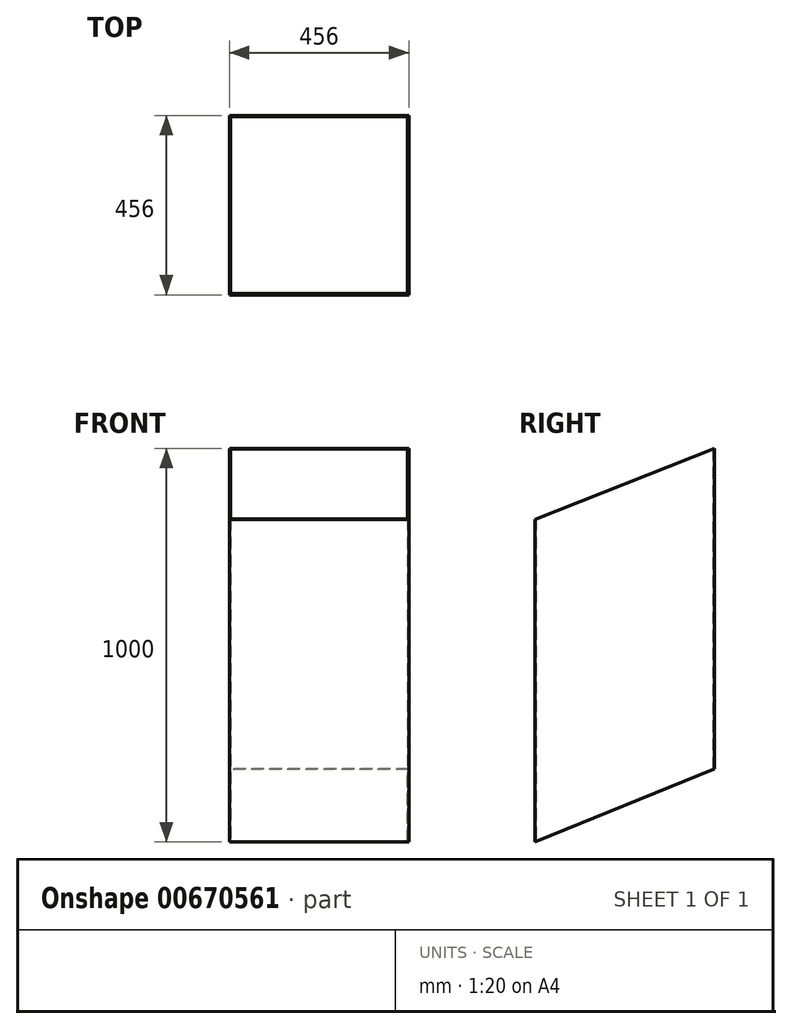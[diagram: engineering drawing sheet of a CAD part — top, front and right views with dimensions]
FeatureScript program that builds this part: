
annotation { "Feature Type Name" : "Feature", "Feature Type Description" : "" }
export const myFeature = defineFeature(function(context is Context, id is Id, definition is map)
    precondition{}
    {
        {
            var Q0;
            Q0=qCreatedBy(makeId("Top.planeOp"),FACE);
            var sketch = newSketch(context, id + "F0", { "sketchPlane" : qUnion([Q0])});
            skLineSegment(sketch, "E0.bottom", {"start": v(225, -225) * mm, "end": v(-225, -225) * mm});
            skLineSegment(sketch, "E0.top", {"start": v(225, 225) * mm, "end": v(-225, 225) * mm});
            skLineSegment(sketch, "E0.left", {"start": v(225, -225) * mm, "end": v(225, 225) * mm});
            skLineSegment(sketch, "E0.right", {"start": v(-225, -225) * mm, "end": v(-225, 225) * mm});
            skPoint(sketch, "E0.middle", {"position": v(0, 0) * mm});
            skLineSegment(sketch, "E1.0", {"start": v(228, 228) * mm, "end": v(-228, 228) * mm});
            skLineSegment(sketch, "E1.1", {"start": v(228, -228) * mm, "end": v(228, 228) * mm});
            skLineSegment(sketch, "E1.2", {"start": v(228, -228) * mm, "end": v(-228, -228) * mm});
            skLineSegment(sketch, "E1.3", {"start": v(-228, -228) * mm, "end": v(-228, 228) * mm});
            skSolve(sketch);
        }
        {
            var Q0;
            Q0=qCreatedBy(makeId("Right.planeOp"),FACE);
            var sketch = newSketch(context, id + "F1", { "sketchPlane" : qUnion([Q0])});
            skLineSegment(sketch, "E2.bottom", {"start": v(228, -174) * mm, "end": v(-228, -174) * mm});
            skLineSegment(sketch, "E2.top", {"start": v(228, 186) * mm, "end": v(-228, 186) * mm});
            skLineSegment(sketch, "E2.left", {"start": v(228, -174) * mm, "end": v(228, 186) * mm});
            skLineSegment(sketch, "E2.right", {"start": v(-228, -174) * mm, "end": v(-228, 186) * mm});
            skPoint(sketch, "E2.middle", {"position": v(0, 6) * mm});
            skLineSegment(sketch, "E3", {"start": v(-228, 0) * mm, "end": v(228, 186) * mm});
            skSolve(sketch);
        }
        {
            var Q0;
            Q0=makeQuery(id+"F0.imprint","IMPRINT",FACE,{"disambiguationData":[TD([[makeQuery(id+"F0.imprint","IMPRINT",EDGE,{"derivedFrom":sQuery(id+"F0.wireOp",EDGE,"E0.bottom")}),1.0]])]});
            extrude(context, id + "F2", {"entities" : qUnion([Q0]), "depth" : 1000 * mm, "offsetDistance" : 25 * mm});
        }
        {
            var Q0;
            {var subQ0=sQuery(id+"F1.wireOp",EDGE,"E2.bottom");Q0=makeQuery(id+"F1.imprint","IMPRINT",FACE,{"disambiguationData":[TD([[makeQuery(id+"F1.imprint","IMPRINT",EDGE,{"derivedFrom":subQ0}),-1.0]])]});}
            extrude(context, id + "F3", {"entities" : qUnion([Q0]), "operationType" : NewBodyOperationType.REMOVE, "endBound" : BoundingType.THROUGH_ALL, "depth" : 25 * mm, "offsetDistance" : 25 * mm, "hasSecondDirection" : true, "secondDirectionBound" : SecondDirectionBoundingType.THROUGH_ALL, "secondDirectionOppositeDirection" : true, "secondDirectionDepth" : 25 * mm});
        }
        {
            var Q0;
            Q0=makeQuery(id+"F2.opExtrude","SWEPT_FACE",FACE,{"disambiguationData":[OSD([sQuery(id+"F0.wireOp",EDGE,"E1.1")])]});
            var sketch = newSketch(context, id + "F4", { "sketchPlane" : qUnion([Q0])});
            skLineSegment(sketch, "E4.bottom", {"start": v(228, 820) * mm, "end": v(-228, 820) * mm});
            skLineSegment(sketch, "E4.top", {"start": v(228, 1180) * mm, "end": v(-228, 1180) * mm});
            skLineSegment(sketch, "E4.left", {"start": v(228, 820) * mm, "end": v(228, 1180) * mm});
            skLineSegment(sketch, "E4.right", {"start": v(-228, 820) * mm, "end": v(-228, 1180) * mm});
            skPoint(sketch, "E4.middle", {"position": v(0, 1000) * mm});
            skLineSegment(sketch, "E5", {"start": v(228, 1000) * mm, "end": v(-228, 820) * mm});
            skSolve(sketch);
        }
        {
            var Q0;
            {var subQ3=sQuery(id+"F4.wireOp",EDGE,"E5");Q0=makeQuery(id+"F4.imprint","IMPRINT",FACE,{"disambiguationData":[TD([[makeQuery(id+"F4.imprint","IMPRINT",EDGE,{"derivedFrom":subQ3}),-1.0]])]});}
            extrude(context, id + "F5", {"entities" : qUnion([Q0]), "operationType" : NewBodyOperationType.REMOVE, "endBound" : BoundingType.THROUGH_ALL, "oppositeDirection" : true, "depth" : 25 * mm, "offsetDistance" : 25 * mm});
        }
    });
